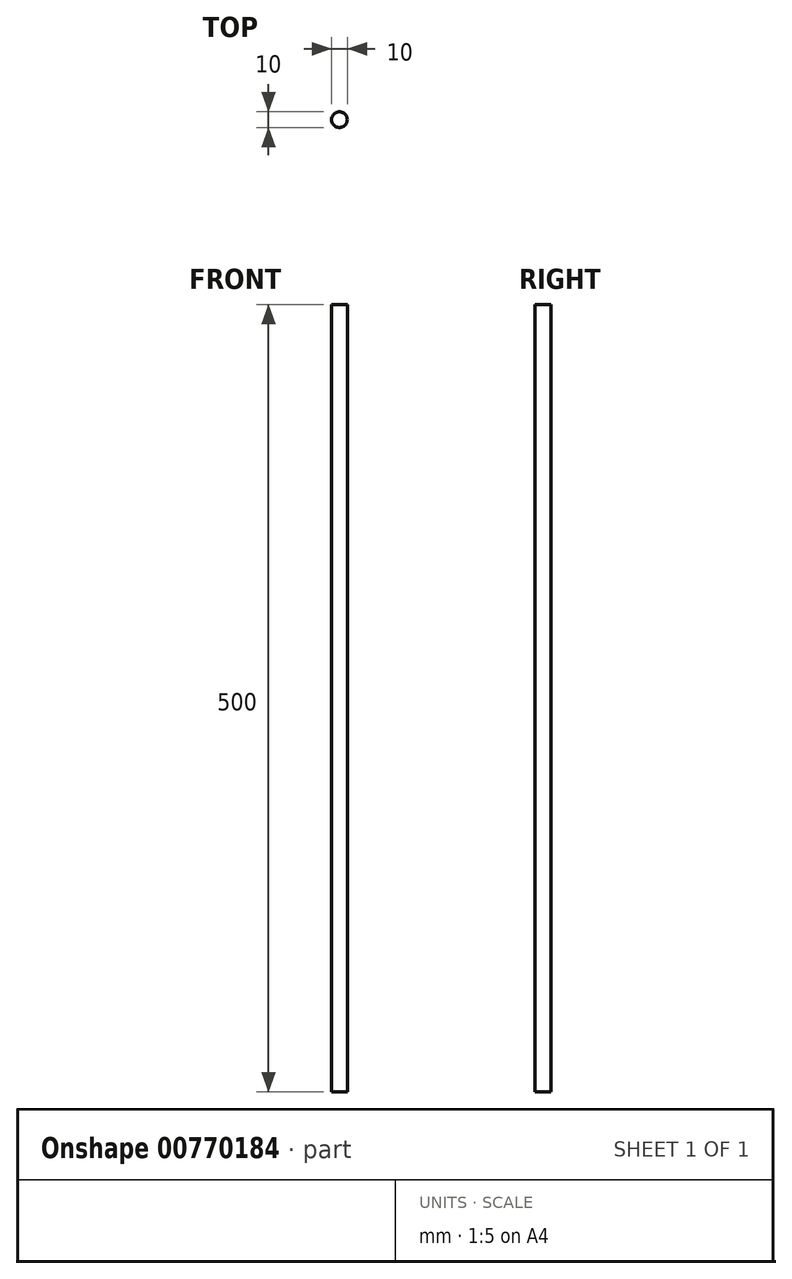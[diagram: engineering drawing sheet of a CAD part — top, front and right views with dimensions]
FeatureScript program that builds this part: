
annotation { "Feature Type Name" : "Feature", "Feature Type Description" : "" }
export const myFeature = defineFeature(function(context is Context, id is Id, definition is map)
    precondition{}
    {
        {
            var Q0;
            Q0=qCreatedBy(makeId("Top.planeOp"),FACE);
            var sketch = newSketch(context, id + "F0", { "sketchPlane" : qUnion([Q0])});
            skCircle(sketch, "E0", {"center": v(0, 0) * mm, "radius": 5 * mm});
            skSolve(sketch);
        }
        {
            var Q0;
            Q0=makeQuery(id+"F0.imprint","IMPRINT",FACE,{"disambiguationData":[TD([[makeQuery(id+"F0.imprint","IMPRINT",EDGE,{"derivedFrom":sQuery(id+"F0.wireOp",EDGE,"E0")}),1.0]])]});
            extrude(context, id + "F1", {"entities" : qUnion([Q0]), "depth" : 500 * mm, "offsetDistance" : 25 * mm});
        }
    });
